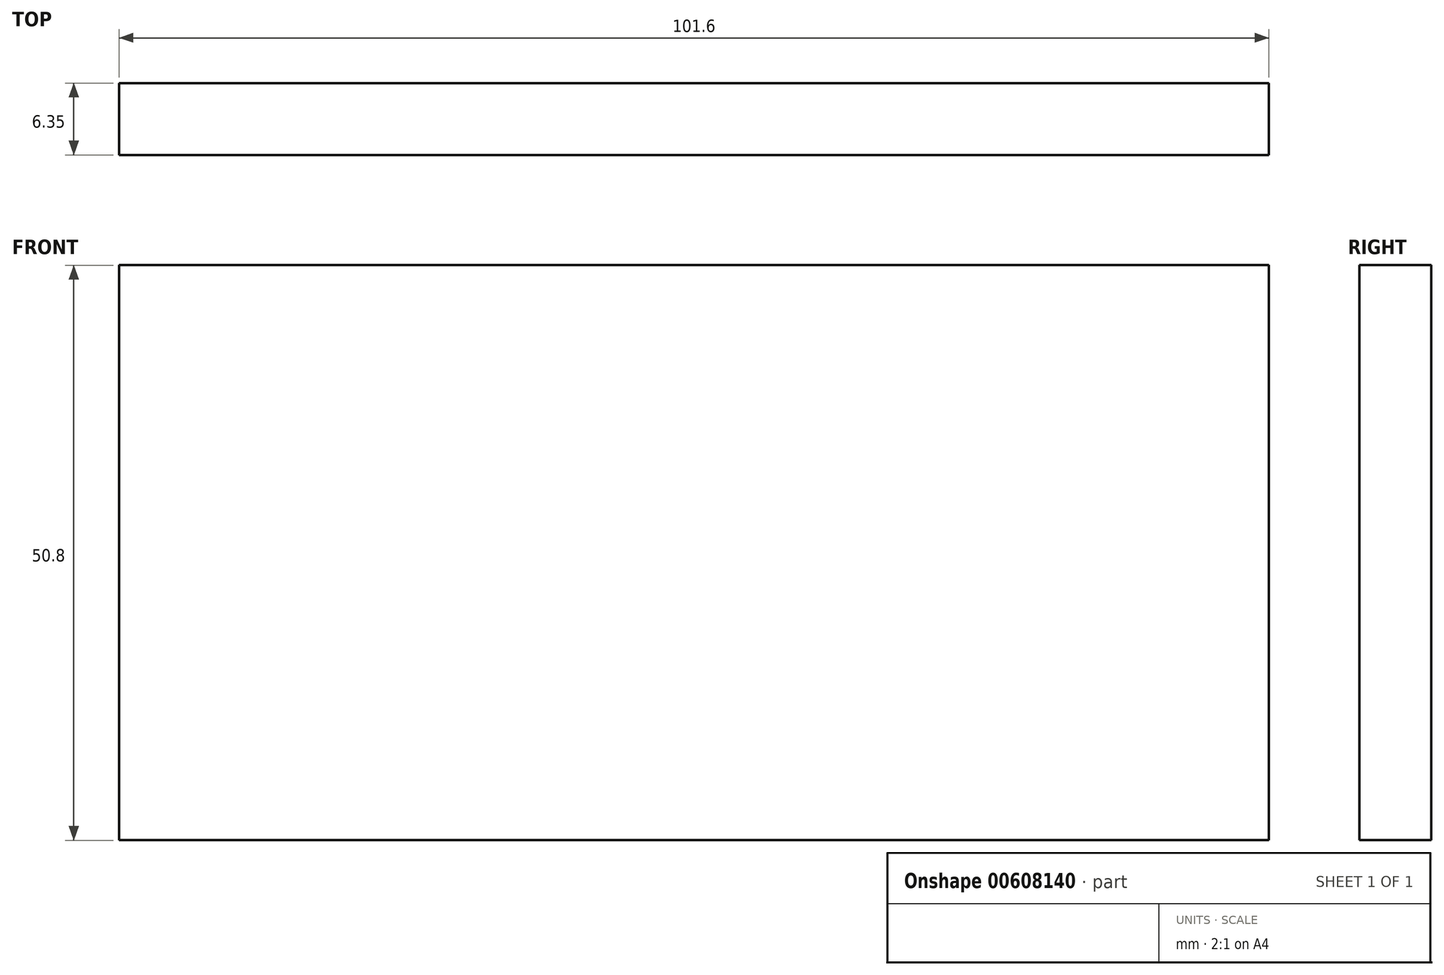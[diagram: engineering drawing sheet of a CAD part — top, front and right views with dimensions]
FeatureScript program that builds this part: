
annotation { "Feature Type Name" : "Feature", "Feature Type Description" : "" }
export const myFeature = defineFeature(function(context is Context, id is Id, definition is map)
    precondition{}
    {
        {
            var Q0;
            Q0=qCreatedBy(makeId("Front.planeOp"),FACE);
            var sketch = newSketch(context, id + "F0", { "sketchPlane" : qUnion([Q0])});
            skLineSegment(sketch, "E0.bottom", {"start": v(-52.77, 38.46) * mm, "end": v(48.83, 38.46) * mm});
            skLineSegment(sketch, "E0.top", {"start": v(-52.77, -12.34) * mm, "end": v(48.83, -12.34) * mm});
            skLineSegment(sketch, "E0.left", {"start": v(-52.77, 38.46) * mm, "end": v(-52.77, -12.34) * mm});
            skLineSegment(sketch, "E0.right", {"start": v(48.83, 38.46) * mm, "end": v(48.83, -12.34) * mm});
            skSolve(sketch);
        }
        {
            var Q0;
            Q0=makeQuery(id+"F0.imprint","IMPRINT",FACE,{"disambiguationData":[TD([[makeQuery(id+"F0.imprint","IMPRINT",EDGE,{"derivedFrom":sQuery(id+"F0.wireOp",EDGE,"E0.bottom")}),-1.0]])]});
            extrude(context, id + "F1", {"entities" : qUnion([Q0]), "depth" : 6.35 * mm, "offsetDistance" : 25.4 * mm});
        }
    });
